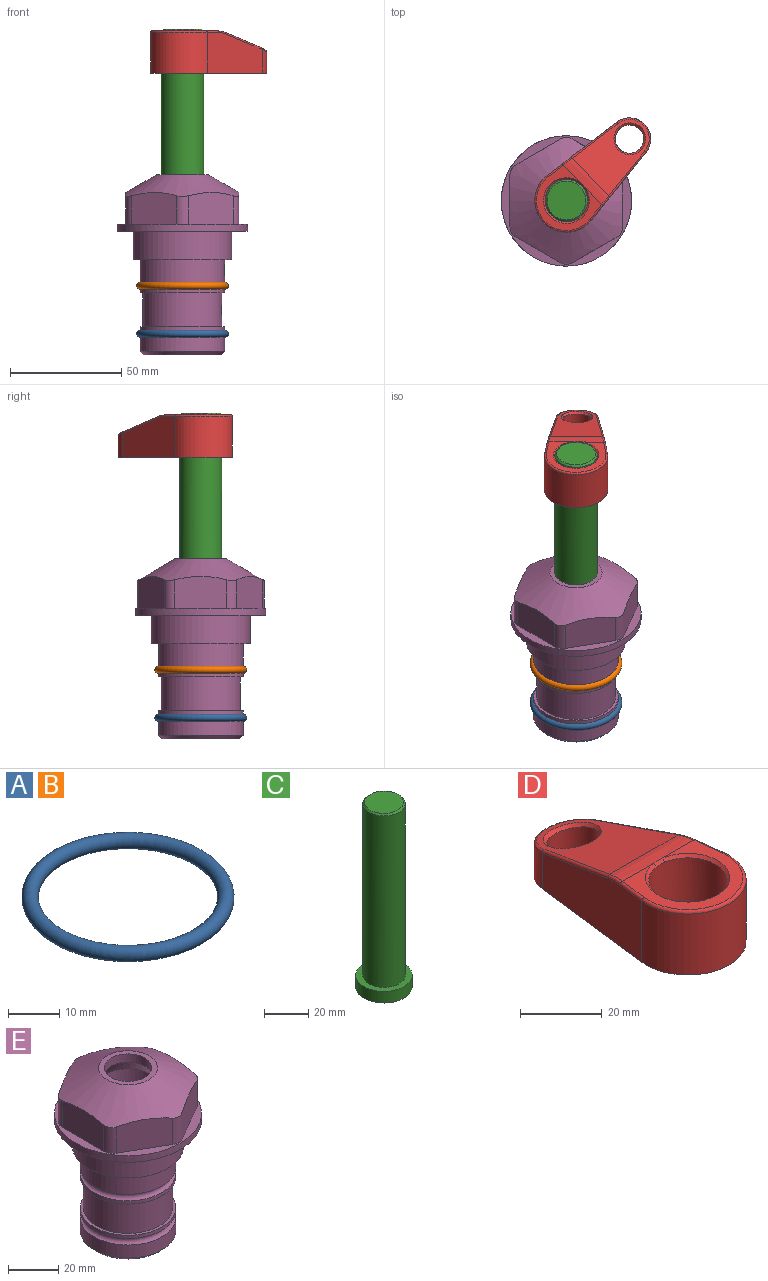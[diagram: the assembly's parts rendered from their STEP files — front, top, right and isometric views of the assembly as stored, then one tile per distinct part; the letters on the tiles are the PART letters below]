
ASSEMBLY  parts=5 mates=4
PART A: 1 faces, bbox 44.7x44.7x3.2 mm
  f0: torus R=19.05mm, axis (0,0,1), area 1193.9mm2
PART B: same geometry as A
PART C: 6 faces, bbox 25.4x25.4x101.6 mm
  f0: plane 17.46x17.46mm, normal (0,0,1), area 239.5mm2, adj f5
  f1: plane 25.4x25.4mm, normal (0,0,-1), area 506.7mm2, adj f2
  f2: cylinder r=12.7mm len=25.4mm, axis (0,0,1), area 506.7mm2, adj f1,f3
  f3: plane 25.4x25.4mm, normal (0,0,1), area 221.7mm2, adj f2,f4
  f4: cylinder r=9.53mm len=94.46mm, axis (0,0,1), area 5653mm2, adj f3,f5
  f5: cone r=8.73mm half-angle=45deg, axis (0,0,-1), area 64.4mm2, adj f0,f4
PART D: 31 faces, bbox 31.7x65.5x19.8 mm
  f0: plane 39.12x18.26mm, normal (0.99,0.12,0), area 612.2mm2, adj f1,f4,f7,f11,f13,f15
  f1: cylinder r=9.53mm len=18.91mm, axis (0,0,-1), area 296.1mm2, adj f0,f2,f7,f17
  f2: plane 39.12x18.26mm, normal (-0.99,0.12,0), area 612.2mm2, adj f1,f4,f7,f12,f14,f16
  f3: cylinder r=6.35mm len=12.7mm, axis (0,0,-1), area 362.4mm2, adj f7,f18
  f4: cylinder r=14.29mm len=28.58mm, axis (0,0,-1), area 882.2mm2, adj f0,f2,f7,f10
  f5: cylinder r=9.53mm len=19.05mm, axis (0,0,-1), area 1092.6mm2, adj f7,f19,f20
  f6: plane 26.99x23.69mm, normal (0,0,1), area 216.2mm2, adj f9,f10,f11,f12,f19
  f7: plane 63.5x28.58mm, normal (0,0,-1), area 661.8mm2, adj f0,f1,f2,f3,f4,f5,f22,f23
  f8: plane 33.52x23.6mm, normal (0,0.26,0.97), area 486mm2, adj f9,f15,f16,f17,f18
  f9: cylinder r=19.05mm len=24.72mm, axis (1,0,0), area 120.4mm2, adj f6,f8,f13,f14,f20
  f10: torus R=13.49mm, axis (0,0,1), area 59mm2, adj f4,f6,f11,f12
  f11: cylinder r=0.79mm len=8.67mm, axis (0.12,-0.99,0), area 10.8mm2, adj f0,f6,f10,f13
  f12: cylinder r=0.79mm len=8.67mm, axis (0.12,0.99,0), area 10.8mm2, adj f2,f6,f10,f14
  f13: bspline ~4.95x1.42mm, area 6.1mm2, adj f0,f9,f11,f15
  f14: bspline ~4.95x1.42mm, area 6.1mm2, adj f2,f9,f12,f16
  f15: cylinder r=0.79mm len=25.95mm, axis (0.12,-0.96,0.26), area 32.9mm2, adj f0,f8,f13,f17
  f16: cylinder r=0.79mm len=25.95mm, axis (0.12,0.96,-0.26), area 32.9mm2, adj f2,f8,f14,f17
  f17: bspline ~18.91x8.38mm, area 30mm2, adj f1,f8,f15,f16
  f18: bspline ~14.29x14.29mm, area 48.3mm2, adj f3,f8
  f19: cone r=9.53mm half-angle=45deg, axis (0,0,1), area 66.5mm2, adj f5,f6,f20
  f20: bspline ~3.22x0.96mm, area 3.5mm2, adj f5,f9,f19
  f21: plane 2.75x2.72mm, normal (0,0,-1), area 2.9mm2, adj f23,f25,f28
  f22: plane 23.05x15.88mm, normal (-0.99,-0.12,0), area 323.6mm2, adj f7,f25,f26,f27,f28,f29
  f23: plane 23.05x15.88mm, normal (0.99,-0.12,0), area 323.6mm2, adj f7,f21,f25,f27,f28,f30
  f24: cylinder r=9.53mm len=10.69mm, axis (0,0,-1), area 114.7mm2, adj f7,f27,f29,f30
  f25: cylinder r=12.7mm len=20.59mm, axis (0,0,-1), area 381.1mm2, adj f7,f21,f22,f23,f26,f28
  f26: plane 2.75x2.72mm, normal (0,0,-1), area 2.9mm2, adj f22,f25,f28
  f27: plane 19.72x18.37mm, normal (0,-0.26,-0.97), area 291.8mm2, adj f22,f23,f24,f28,f29,f30
  f28: cylinder r=15.88mm len=19.92mm, axis (1,0,0), area 54.8mm2, adj f21,f22,f23,f25,f26,f27
  f29: cylinder r=1.59mm len=11mm, axis (0,0,-1), area 34.7mm2, adj f7,f22,f24,f27
  f30: cylinder r=1.59mm len=11mm, axis (0,0,-1), area 34.7mm2, adj f7,f23,f24,f27
PART E: 36 faces, bbox 58.7x58.7x81 mm
  f0: cylinder r=17.78mm len=35.56mm, axis (0,0,1), area 1670.8mm2, adj f23,f24,f31
  f1: cylinder r=19.05mm len=38.1mm, axis (0,0,1), area 1191.9mm2, adj f26,f27,f30
  f2: plane 58.66x58.66mm, normal (0,0,-1), area 1150.6mm2, adj f3,f28
  f3: cylinder r=29.33mm len=58.66mm, axis (0,0,-1), area 585.1mm2, adj f2,f4
  f4: plane 58.66x58.66mm, normal (0,0,1), area 475.9mm2, adj f3,f5,f6,f7,f8,f9,f10,f11
  f5: plane 20.32x14.34mm, normal (-0.5,0.87,0), area 324.4mm2, adj f4,f15,f16,f17
  f6: plane 20.32x14.34mm, normal (0.5,0.87,0), area 324.4mm2, adj f4,f14,f15,f17
  f7: plane 23.48x14.34mm, normal (1,0,0), area 324.4mm2, adj f4,f13,f14,f17
  f8: plane 20.32x14.34mm, normal (0.5,-0.87,0), area 324.4mm2, adj f4,f12,f13,f17
  f9: plane 20.32x14.34mm, normal (-0.5,-0.87,0), area 324.4mm2, adj f4,f11,f12,f17
  f10: plane 23.48x14.34mm, normal (-1,0,0), area 324.4mm2, adj f4,f11,f16,f17
  f11: cylinder r=5.08mm len=12.85mm, axis (0,0,-1), area 67.2mm2, adj f4,f9,f10,f17
  f12: cylinder r=5.08mm len=12.85mm, axis (0,0,-1), area 67.2mm2, adj f4,f8,f9,f17
  f13: cylinder r=5.08mm len=12.85mm, axis (0,0,-1), area 67.2mm2, adj f4,f7,f8,f17
  f14: cylinder r=5.08mm len=12.85mm, axis (0,0,-1), area 67.2mm2, adj f4,f6,f7,f17
  f15: cylinder r=5.08mm len=12.85mm, axis (0,0,-1), area 67.2mm2, adj f4,f5,f6,f17
  f16: cylinder r=5.08mm len=12.85mm, axis (0,0,-1), area 67.2mm2, adj f4,f5,f10,f17
  f17: cone r=11.73mm half-angle=60deg, axis (0,0,-1), area 2071.8mm2, adj f5,f6,f7,f8,f9,f10,f11,f12
  f18: plane 23.46x23.46mm, normal (0,0,1), area 147.4mm2, adj f17,f35
  f19: plane 34.93x34.93mm, normal (0,0,-1), area 958mm2, adj f29
  f20: cylinder r=19.05mm len=38.1mm, axis (0,0,1), area 760.1mm2, adj f21,f29
  f21: torus R=19.05mm, axis (0,0,1), area 565.3mm2, adj f20,f22
  f22: cylinder r=19.05mm len=38.1mm, axis (0,0,1), area 190mm2, adj f21,f23
  f23: plane 38.1x38.1mm, normal (0,0,1), area 146.9mm2, adj f0,f22
  f24: plane 38.1x38.1mm, normal (0,0,-1), area 146.9mm2, adj f0,f25
  f25: cylinder r=19.05mm len=38.1mm, axis (0,0,1), area 190mm2, adj f24,f26
  f26: torus R=19.05mm, axis (0,0,1), area 565.3mm2, adj f1,f25
  f27: plane 44.45x44.45mm, normal (0,0,-1), area 411.7mm2, adj f1,f28
  f28: cylinder r=22.23mm len=44.45mm, axis (0,0,1), area 1773.5mm2, adj f2,f27
  f29: cone r=19.05mm half-angle=45deg, axis (0,0,1), area 257.5mm2, adj f19,f20
  f30: cylinder r=3.17mm len=6.75mm, axis (-1,0,0), area 128mm2, adj f1,f33
  f31: cylinder r=3.17mm len=6.35mm, axis (-1,0,0), area 102.5mm2, adj f0,f33
  f32: plane 25.4x25.4mm, normal (0,0,1), area 506.7mm2, adj f33
  f33: cylinder r=12.7mm len=66.42mm, axis (0,0,-1), area 5236.2mm2, adj f30,f31,f32,f34
  f34: cone r=9.53mm half-angle=30deg, axis (0,0,-1), area 443.4mm2, adj f33,f35
  f35: cylinder r=9.53mm len=19.05mm, axis (0,0,-1), area 240.9mm2, adj f18,f34
PLACE A t=(0,0,-21.59)mm
PLACE B at identity
PLACE C rot(axis=(0,0,-1),45.7deg) t=(0,0,27.55)mm
PLACE D rot(axis=(0,0,-1),45.7deg) t=(0,0,26.76)mm
PLACE E at identity fixed
MATE fastened E.f0 <-> B.f0  axis (0,0,1) through (0,0,-24.51)mm
MATE fastened D.f4 <-> C.f2  axis (0,0,1) through (0,0,90.26)mm
MATE fastened E.f0 <-> A.f0  axis (0,0,1) through (0,0,-46.1)mm
MATE cylindrical C.f2 <-> E.f0  axis (0,0,-1) through (0,0,-10.55)mm
